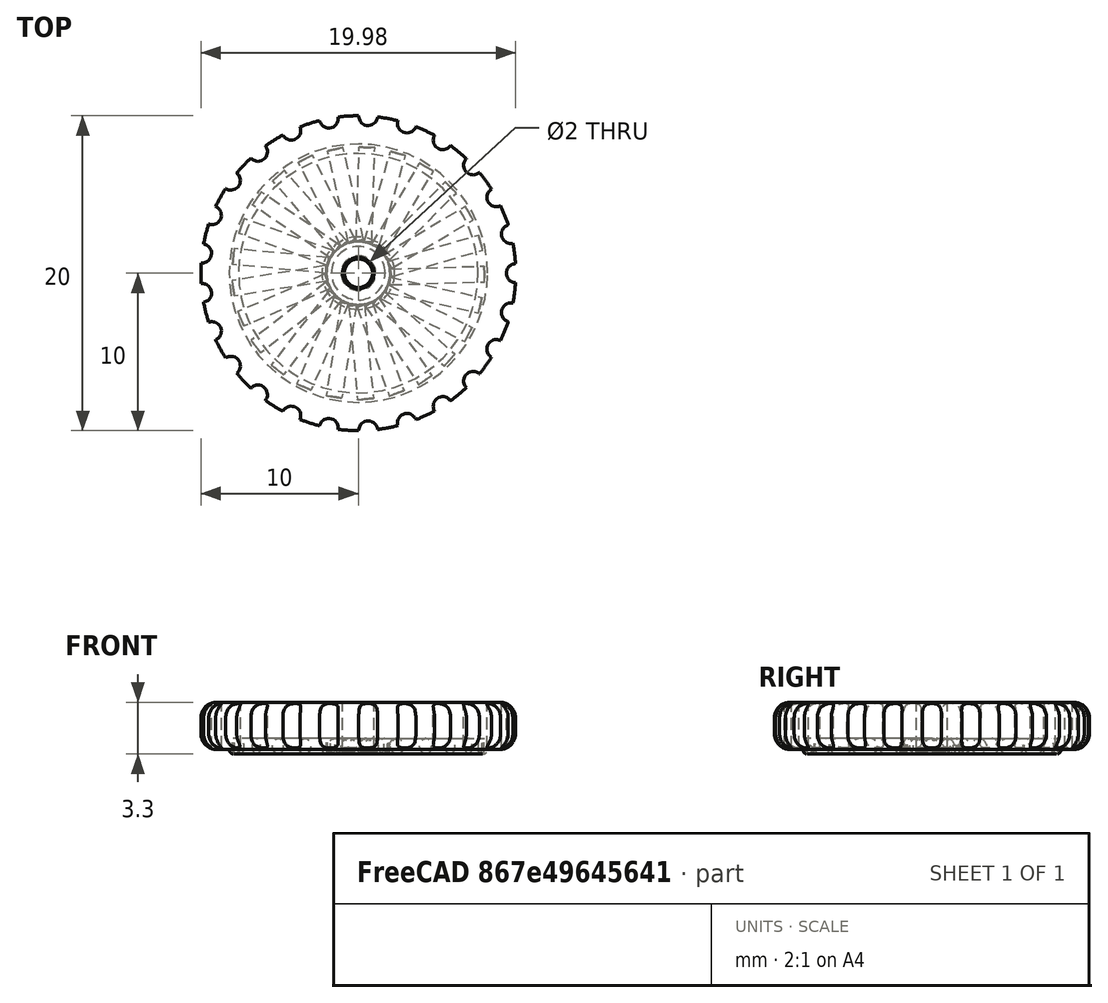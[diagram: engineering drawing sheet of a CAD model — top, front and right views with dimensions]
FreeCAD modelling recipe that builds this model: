
FCSTD DOCUMENT  (FreeCAD 0.18R4 (GitTag))
Label: Rueda a medida reto (prueba)
License: All rights reserved
LicenseURL: http://en.wikipedia.org/wiki/All_rights_reserved
objects: Part::Cylinder×4, Part::Torus×3, Part::FeaturePython×2, Part::Cut×2, Part::Fillet×1, Part::Fuse×1, Part::MultiFuse×1
note: 14 computed .brp shape members not serialized (recipe doc carries the construction recipe); baked Part::Feature solids carry a one-line shape summary decoded from their .brp

FEATURE [Part::Cylinder] Cylinder  label="Cilindro"
  Angle = 360
  AttacherType = Attacher::AttachEngine3D
  Height = 3
  Radius = 10
FEATURE [Part::Fillet] Fillet
  Base = -> Cylinder
  Edges = 2 edges r=1: [Edge1,Edge3]
FEATURE [Part::Cylinder] Cylinder001  label="Cilindro001"
  Angle = 360
  AttacherType = Attacher::AttachEngine3D
  Height = 10
  Placement = pos=(10,0,0) rot=(0,0,1;0rad)
  Radius = 0.6
FEATURE [Part::FeaturePython] Array  # Draft array (typed FeaturePython)
  Angle = 360
  ArrayType = 1
  Axis = (0,0,1)
  Base = -> Cylinder001
  Center = (0,0,0)
  Fuse = false
  IntervalAxis = (0,0,0)
  IntervalX = (1,0,0)
  IntervalY = (0,1,0)
  IntervalZ = (0,0,1)
  NumberPolar = 25
  NumberX = 2
  NumberY = 2
  NumberZ = 1
FEATURE [Part::Cut] Cut
  Base = -> Fillet
  Refine = true
  Tool = -> Array
FEATURE [Part::Cylinder] Cylinder002  label="Cilindro002"
  Angle = 360
  AttacherType = Attacher::AttachEngine3D
  Height = 10
  Radius = 1
FEATURE [Part::Cut] Cut001
  Base = -> Cut
  Refine = true
  Tool = -> Cylinder002
FEATURE [Part::Torus] Torus  label="Toro"
  Angle1 = -180
  Angle2 = 180
  Angle3 = 360
  AttacherType = Attacher::AttachEngine3D
  Radius1 = 1
  Radius2 = 0.1
FEATURE [Part::Fuse] Fusion
  Base = -> Cut001
  Refine = true
  Tool = -> Torus
FEATURE [Part::Cylinder] Cylinder003  label="Cilindro003"
  Angle = 360
  AttacherType = Attacher::AttachEngine3D
  Height = 6
  Placement = pos=(1.62635,1.20208,0.2) rot=(0.357407,-0.862856,-0.357407;4.56541rad)
  Radius = 0.5
FEATURE [Part::FeaturePython] Array001  # Draft array (typed FeaturePython)
  Angle = 360
  ArrayType = 1
  Axis = (0,0,1)
  Base = -> Cylinder003
  Center = (0,0,0)
  Fuse = false
  IntervalAxis = (0,0,0)
  IntervalX = (1,0,0)
  IntervalY = (0,1,0)
  IntervalZ = (0,0,1)
  NumberPolar = 25
  NumberX = 2
  NumberY = 2
  NumberZ = 1
FEATURE [Part::Torus] Torus001  label="Toro001"
  Angle1 = -180
  Angle2 = 180
  Angle3 = 360
  AttacherType = Attacher::AttachEngine3D
  Radius1 = 2
  Radius2 = 0.3
FEATURE [Part::Torus] Torus002  label="Toro002"
  Angle1 = -180
  Angle2 = 180
  Angle3 = 360
  AttacherType = Attacher::AttachEngine3D
  Radius1 = 7.9
  Radius2 = 0.3
FEATURE [Part::MultiFuse] Fusion001
  Refine = true
  Shapes = -> [Fusion,Torus002,Torus001]
